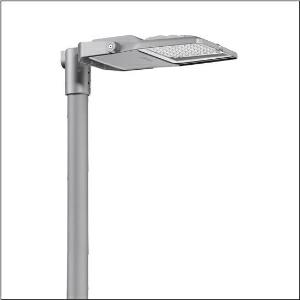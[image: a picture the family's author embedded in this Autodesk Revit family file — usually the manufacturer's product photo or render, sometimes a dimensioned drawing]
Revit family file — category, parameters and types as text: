
# Revit family: floodlight_fl_21_iq_mini___pl61_5xa7771c2c3a_2691
name_source: partatom
category: Lighting Fixtures
units: mm (PartAtom-declared; Revit-internal decimal feet)

## family parameters
Cut with Voids When Loaded = No
Host = Face
Light Source = No
Part Type = Normal
Room Calculation Point = No
Round Connector Dimension = Use Diameter
Shared = No

## types (1)
- --- (1 x LED, 11980 lm, 87.2 W, 3000K)
    Apparent Load = 87 VA
    CIE Flux Codes = 33 65 98 100 100
    Color Rendering = 70
    Color Temperature = 3000K
    Default Elevation = 1800 mm
    Description = Floodlight FL 21 iQ mini, floodlight, primary light control with lens, of PMMA, primary optical cover: protective disc, of toughened safety glass, transparent, light distribution: PL61, light emission: direct distribution, installation type: surface-mounted, LED, High Power LED, rated luminous flux: 11.980lm, luminous efficacy: 137lm/W, light colour: 730, colour temperature: 3000K, control: Auto-Match, Temp-Guard, Lumen-Switch, Night-Set, Smart-Wire, Light-Fading, Desk-Remote (wireless, voltage-free reading and setting of iQ features in the workshop via application-optimized NFC function/RFID function), optimised constant luminous flux control (CLO 2.0), with terminal, 6-pole, mains connection: 220..240V, AC, 50/60Hz, start of lifetime: 87W, end of service life: 92W, reduction: 40W, luminaire housing, of diecast aluminium, powder-coated, Siteco® metallic grey (DB 702S), corrosivity category C5 mid according to DIN EN ISO 12944, sealing non-destructively replaceable, please order mast flange separately, mast bracket, of steel, galvanised, powder-coated, Siteco® metallic grey (DB 702S), protection rating (complete): IP66, insulation class (complete): insulation class II (safety insulation), certification: CE, ENEC, VDE, protection symbol: D, impact resistance: IK08, permissible operating ambient temperature: -40..+40°C, permissible operating ambient temperature for outdoor applications: -40..+50°C, standard: DIN EN 12944, LABS conformity tested according to VDMA 24364:2018-05, packaging unit: 1 piece

Light Distribution: PL61
    Height = 70 mm
    Lamp = 1 x LED
    Lamp Light Flux = 11980 lm
    Lamp Power = 87.2 W
    Lamp count = 1
    Length = 485 mm
    Luminous efficacy = 137 lm/W
    Manufacturer = Siteco
    ModVariant = No
    Model = 5XA7771C2C3A
    Number of Poles = 1
    OnlyDefault = Yes
    Power Factor = 1
    Product Name = Floodlight FL 21 iQ mini | PL61
    Product group = floodlight | pylon annexe
    ProductGroupID = 6200
    Protection Class = Protection class II
    Protection Degree = IP 66
    RLX_Detail_Level = 1
    RLX_Emergency_Light_Flux = 0 lm
    RLX_Emergency_Type = 0
    RLX_Emergency_Type_DB = No
    RlxData = <blob elided: 101373 chars, md5=fe895ad8>
    Socket = socket
    Standby Power = 0 W
    System Light Flux = 11980 lm
    System Power = 87 W
    Type Comments = factory setting: luminous flux: 100 % | dim-lin: 254 | 456 mA
    Type Image = l_1007125.jpg
    URL = http://relux.com
    VarID = @adj_106371
    Voltage = 0 V
    Weight = 0.00 kg
    Width = 337 mm

## geometry (parser evidence)
native form markers: Blend x4, Sweep x11
no freeform markers — native parametric forms only
